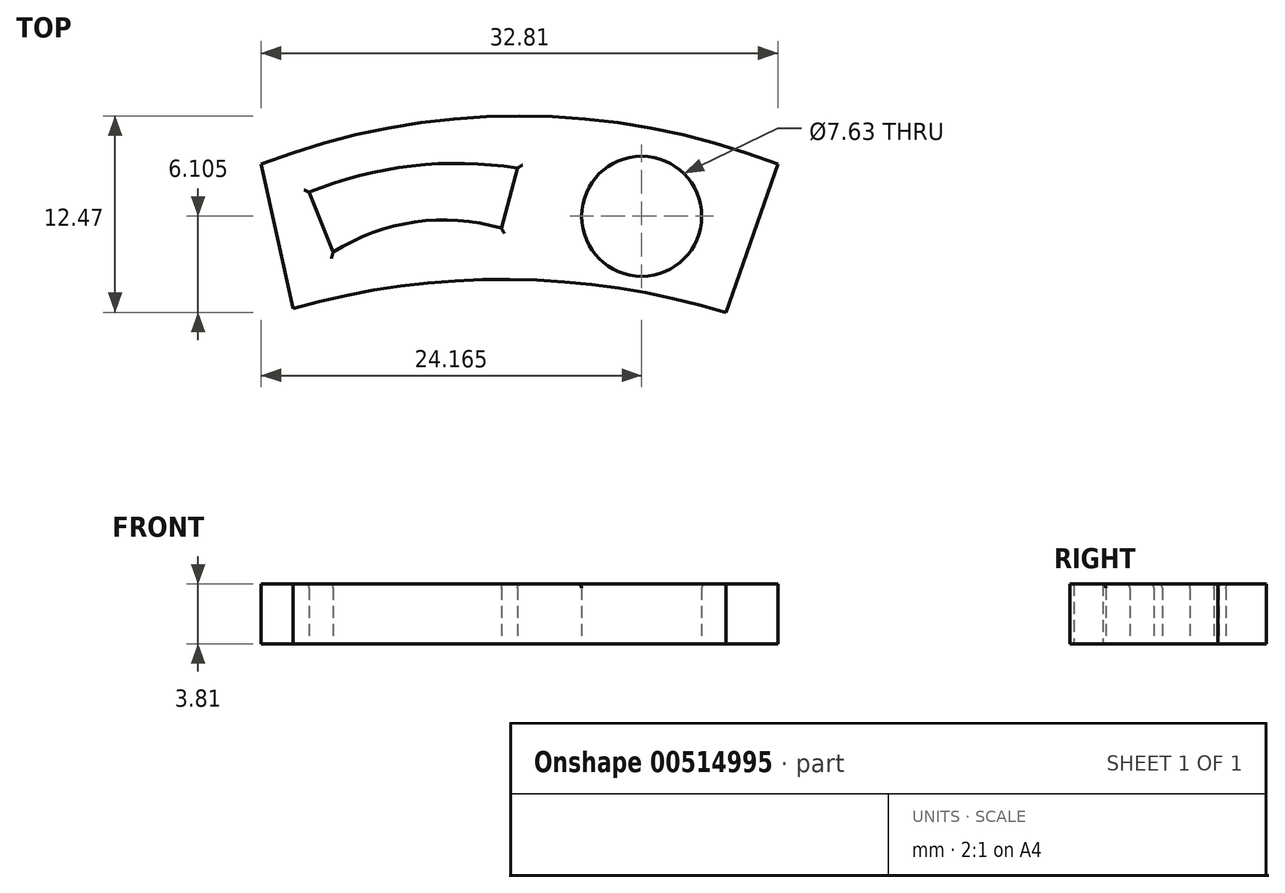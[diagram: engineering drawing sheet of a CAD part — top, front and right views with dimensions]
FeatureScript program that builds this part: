
annotation { "Feature Type Name" : "Feature", "Feature Type Description" : "" }
export const myFeature = defineFeature(function(context is Context, id is Id, definition is map)
    precondition{}
    {
        {
            var Q0;
            Q0=qCreatedBy(makeId("Top.planeOp"),FACE);
            var sketch = newSketch(context, id + "F0", { "sketchPlane" : qUnion([Q0])});
            skArc(sketch, "E0", {"start": v(12.97, -10.56) * mm, "mid": v(-3.43, -7.5) * mm, "end": v(-19.84, -10.56) * mm});
            skArc(sketch, "E1", {"start": v(9.67, -19.97) * mm, "mid": v(-4.05, -17.88) * mm, "end": v(-17.8, -19.72) * mm});
            skLineSegment(sketch, "E2", {"start": v(-19.84, -10.56) * mm, "end": v(-17.8, -19.72) * mm});
            skLineSegment(sketch, "E3", {"start": v(9.67, -19.97) * mm, "end": v(12.97, -10.56) * mm});
            skCircle(sketch, "E4", {"center": v(4.32, -13.87) * mm, "radius": 3.82 * mm});
            skArc(sketch, "E5", {"start": v(-3.56, -10.81) * mm, "mid": v(-10.28, -10.67) * mm, "end": v(-16.8, -12.34) * mm});
            skArc(sketch, "E6", {"start": v(-4.58, -14.63) * mm, "mid": v(-10.09, -14.23) * mm, "end": v(-15.26, -16.15) * mm});
            skLineSegment(sketch, "E7", {"start": v(-16.8, -12.34) * mm, "end": v(-15.26, -16.15) * mm});
            skLineSegment(sketch, "E8", {"start": v(-4.58, -14.63) * mm, "end": v(-3.56, -10.81) * mm});
            skSolve(sketch);
        }
        {
            var Q0;
            Q0=makeQuery(id+"F0.imprint","IMPRINT",FACE,{"disambiguationData":[TD([[makeQuery(id+"F0.imprint","IMPRINT",EDGE,{"derivedFrom":sQuery(id+"F0.wireOp",EDGE,"E0")}),1.0]])]});
            extrude(context, id + "F1", {"entities" : qUnion([Q0]), "depth" : 3.8 * mm, "offsetDistance" : 25.4 * mm});
        }
        {
            var Q0;
            Q0=makeQuery(id+"F1.opExtrude","CAP_EDGE",EDGE,{"disambiguationData":[OSD([sQuery(id+"F0.wireOp",EDGE,"E7")])],"isStart":false});
            var Q1;
            Q1=makeQuery(id+"F1.opExtrude","CAP_EDGE",EDGE,{"disambiguationData":[OSD([sQuery(id+"F0.wireOp",EDGE,"E4")])],"isStart":false});
            var Q2;
            Q2=makeQuery(id+"F1.opExtrude","CAP_EDGE",EDGE,{"disambiguationData":[OSD([sQuery(id+"F0.wireOp",EDGE,"E5")])],"isStart":false});
            var Q3;
            Q3=makeQuery(id+"F1.opExtrude","CAP_EDGE",EDGE,{"disambiguationData":[OSD([sQuery(id+"F0.wireOp",EDGE,"E6")])],"isStart":false});
            var Q4;
            Q4=makeQuery(id+"F1.opExtrude","CAP_EDGE",EDGE,{"disambiguationData":[OSD([sQuery(id+"F0.wireOp",EDGE,"E8")])],"isStart":false});
            fillet(context, id + "F2", {"entities" : qUnion([Q0, Q1, Q2, Q3, Q4]), "radius" : 0.25 * mm, "tangentPropagation" : true, "allowEdgeOverflow" : false});
        }
    });
